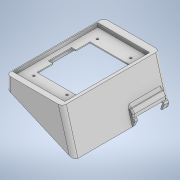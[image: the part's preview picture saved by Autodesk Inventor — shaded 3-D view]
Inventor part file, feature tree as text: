
AUTODESK INVENTOR PART (.ipt)
format: ipt  version: 2022 (Build 260153000, 153)  size: 768,000 bytes
history: native  units: mm
features: extrude x27, sketch x23, projected_geometry x10, sweep x4, fillet x2, plane x1, chamfer x1
ambient origin geometry x8: Origin, YZ Plane, XZ Plane, XY Plane, X Axis, Y Axis, Z Axis, Center Point
bodies: Solid1 (feature_tree)
feature tree (68):
  extrude  "Extrusion1"  Depth=193.2mm
  extrude  "Extrusion2"  Depth=4.2mm
  extrude  "Extrusion3"  Depth=65.697mm
  extrude  "Extrusion4"  Depth=4.2mm
  extrude  "Extrusion5"  Depth=126.501mm
  extrude  "Extrusion6"  Depth=22.6mm
  extrude  "Extrusion7"  Depth=8.0mm
  sweep  "Sweep1"
  plane  "Work Plane1"
  extrude  "Extrusion8"  Depth=11.0mm
  sweep  "Sweep2"
  sketch  "Sketch14"  dims[d10=0.0mm d11=22.6mm]
  extrude  "Extrusion9"  Depth=79.0mm
  sweep  "Sweep4"
  extrude  "Extrusion10"  Depth=40.0mm
  extrude  "Extrusion11"  Depth=9.0mm TaperAngle=0.0deg
  chamfer  "Chamfer1"  Distance=72.0mm
  extrude  "Extrusion12"  Depth=4.083461mm
  extrude  "Extrusion13"  Depth=1000.0mm TaperAngle=0.0deg
  sweep  "Sweep5"
  extrude  "Extrusion14"  Depth=10.0mm
  extrude  "Extrusion15"  Depth=10.0mm TaperAngle=0.0deg
  extrude  "Extrusion24"  Depth=8.0mm
  extrude  "Extrusion25"  TaperAngle=0.0deg  [1 undecoded]
  extrude  "Extrusion26"  TaperAngle=90.0deg  [1 undecoded]
  fillet  "Fillet1"  Radius=2.0mm
  extrude  "Extrusion27"  Depth=10.0mm TaperAngle=0.0deg
  extrude  "Extrusion28"  Depth=10.0mm
  fillet  "Fillet2"  Radius=8.0mm
  extrude  "Extrusion29"  Depth=8.0mm
  extrude  "Extrusion30"  Depth=10.0mm
  extrude  "Extrusion31"  Depth=17.0mm
  extrude  "Extrusion32"  Depth=8.0mm
  extrude  "Extrusion33"  Depth=8.0mm
  extrude  "Extrusion34"  Depth=17.0mm
  extrude  "Extrusion35"  TaperAngle=0.0deg  [1 undecoded]
  sketch  "Sketch1"  dims[d0=110.94mm d1=193.2mm]
  sketch  "Sketch2"  dims[d2=4.2mm d3=4.2mm]
  projected_geometry  "Projected Loop1"
  sketch  "Sketch5"  dims[d4=65.7mm d5=65.697mm]
  projected_geometry  "Projected Loop2"
  projected_geometry  "Projected Loop3"
  sketch  "Sketch8"  dims[d6=4.2mm d7=4.2mm]
  sketch  "3D Sketch1"
  sketch  "Sketch11"  dims[d8=126.2mm d9=126.501mm]
  projected_geometry  "Projected Loop5"
  projected_geometry  "Projected Loop6"
  sketch  "3D Sketch2"
  projected_geometry  "Projected Loop7"
  projected_geometry  "Projected Loop8"
  sketch  "3D Sketch4"
  sketch  "Sketch18"  dims[d12=35.0mm d13=8.0mm]
  sketch  "Sketch23"  dims[d14=2.0mm d15=0.0mm d16=2.0mm]
  sketch  "Sketch24"  dims[d17=14.0mm d18=11.0mm]
  projected_geometry  "Projected Loop11"
  sketch  "3D Sketch5"
  sketch  "Sketch31"  dims[d19=6.0mm d20=7.5mm d21=0.0mm]
  projected_geometry  "Projected Loop14"
  sketch  "Sketch48"  dims[d22=105.0mm d23=79.0mm]
  projected_geometry  "Projected Loop15"
  sketch  "Sketch51"  dims[d24=6.0mm d25=30.0mm]
  sketch  "Sketch52"  dims[d26=40.0mm d27=40.0mm]
  sketch  "Sketch53"  dims[d28=9.0mm d29=7.5mm d30=0.0mm]
  sketch  "Sketch57"  dims[d39=2.0mm d40=72.0mm d41=0.0mm]
  sketch  "Sketch58"  dims[d42=23.5mm d47=4.083461mm]
  sketch  "Sketch60"  dims[d48=140.0mm d49=1000.0mm d50=0.0mm]
  sketch  "Sketch61"  dims[d51=23.1125mm d52=23.113mm]
  sketch  "Sketch62"  dims[d53=63.0mm d54=0.0mm d55=6.0mm d56=1000.0mm d57=0.0mm d58=8.0mm d59=0.0mm d60=0.0mm d62=90.0deg d64=2.0mm d65=1000.0mm d66=0.0mm d80=13.0mm d81=8.0mm d82=8.0mm d83=13.0mm d84=17.0mm d85=8.0mm d86=8.0mm d87=17.0mm d88=0.0mm d89=0.0mm d90=13.0mm d91=8.0mm d92=13.0mm d93=8.0mm d96=10.0mm d97=0.0mm d98=0.0mm d99=0.0mm d100=1000.0mm d101=0.0mm d102=4.2mm d103=5.5mm d104=13.0mm d105=4.2mm d106=4.2mm d107=4.2mm d108=10.0mm d109=5.5mm d110=5.5mm d111=10.0mm d112=13.0mm d113=5.5mm d114=9.0mm d115=0.0mm d116=0.8mm d117=2.0mm d118=45.0deg d121=9.0mm d122=0.0mm d123=10.0mm d124=0.0mm d127=2.0mm d128=0.0mm d129=0.0mm d130=1000.0mm d131=0.0mm d133=71.586mm d134=67.15mm d135=0.0mm d136=0.0mm d137=16.0mm d138=0.0mm d175=14.17mm d176=3.0mm d178=5.0mm d179=20.100957mm d180=10.0mm d183=2.0mm d184=20.100957mm d185=3.2mm d187=2.0mm d188=8.0mm d189=10.0mm d190=0.0mm d191=2.0mm d192=0.0mm d193=2.0mm d194=0.0mm d195=3.0mm d196=2.0mm d197=0.0mm d198=9.0mm d199=5.65mm d200=10.0mm d201=0.0mm d202=3.0mm d203=9.0mm d204=8.5mm d205=1.5mm d206=0.0mm d207=5.8mm d208=13.4mm d209=16.0mm d210=1.5mm d211=1.3mm d212=1.5mm d213=0.0mm d216=0.0mm d217=7.4mm d218=2.3mm d222=135.0deg d223=135.0deg d224=1.314871mm d225=1.314871mm d226=8.0mm d227=19.049mm d228=3.3mm d229=10.0mm d230=0.0mm d231=15.8mm d232=4.2mm d233=4.2mm d234=3.6mm d235=1.0mm d236=1.0mm d237=1.0mm d238=1.5mm d239=0.0mm d241=22.597mm d242=10.0mm d243=0.0mm d244=1000.0mm d245=0.0mm d246=10.0mm d247=0.0mm]
note: 3 required parameter values undecoded (feature->parameter linkage not recoverable at this tier; creation-order binding heuristic only, values carry confidence <= 0.55)
